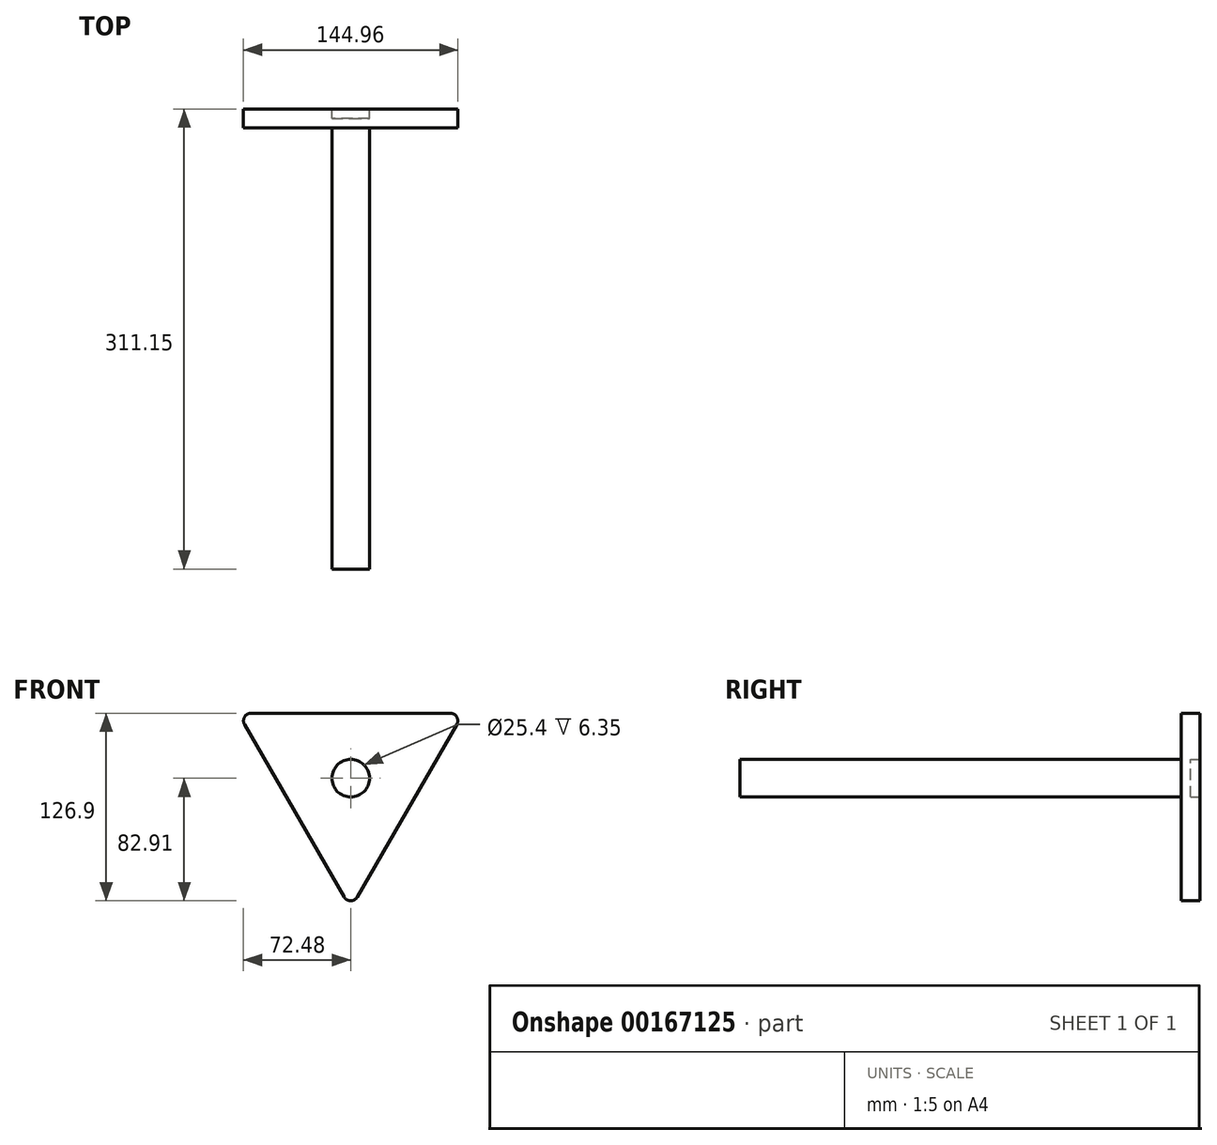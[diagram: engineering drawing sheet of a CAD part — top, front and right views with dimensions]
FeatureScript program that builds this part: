
annotation { "Feature Type Name" : "Feature", "Feature Type Description" : "" }
export const myFeature = defineFeature(function(context is Context, id is Id, definition is map)
    precondition{}
    {
        {
            var Q0;
            Q0=qCreatedBy(makeId("Front.planeOp"),FACE);
            var sketch = newSketch(context, id + "F0", { "sketchPlane" : qUnion([Q0])});
            skLineSegment(sketch, "E0.0", {"start": v(-76.2, 44) * mm, "end": v(76.2, 44) * mm});
            skLineSegment(sketch, "E0.1", {"start": v(76.2, 44) * mm, "end": v(0, -87.99) * mm});
            skLineSegment(sketch, "E0.2", {"start": v(0, -87.99) * mm, "end": v(-76.2, 44) * mm});
            skCircle(sketch, "E1", {"center": v(0, 0) * mm, "radius": 12.7 * mm});
            skSolve(sketch);
        }
        {
            var Q0;
            Q0=makeQuery(id+"F0.imprint","IMPRINT",FACE,{"disambiguationData":[TD([[makeQuery(id+"F0.imprint","IMPRINT",EDGE,{"derivedFrom":sQuery(id+"F0.wireOp",EDGE,"E0.0")}),-1.0]])]});
            extrude(context, id + "F1", {"entities" : qUnion([Q0]), "endBound" : BoundingType.SYMMETRIC, "depth" : 12.7 * mm});
        }
        {
            var Q0;
            Q0=makeQuery(id+"F1.opExtrude","SWEPT_EDGE",EDGE,{"disambiguationData":[OSD([sQuery(id+"F0.wireOp",EDGE,"E0.1"),sQuery(id+"F0.wireOp",EDGE,"E0.2")])]});
            var Q1;
            Q1=makeQuery(id+"F1.opExtrude","SWEPT_EDGE",EDGE,{"disambiguationData":[OSD([sQuery(id+"F0.wireOp",EDGE,"E0.0"),sQuery(id+"F0.wireOp",EDGE,"E0.1")])]});
            var Q2;
            Q2=makeQuery(id+"F1.opExtrude","SWEPT_EDGE",EDGE,{"disambiguationData":[OSD([sQuery(id+"F0.wireOp",EDGE,"E0.0"),sQuery(id+"F0.wireOp",EDGE,"E0.2")])]});
            fillet(context, id + "F2", {"entities" : qUnion([Q0, Q1, Q2]), "radius" : 5.08 * mm, "tangentPropagation" : true, "allowEdgeOverflow" : false});
        }
        {
            var Q0;
            Q0=makeQuery(id+"F0.imprint","IMPRINT",FACE,{"disambiguationData":[TD([[makeQuery(id+"F0.imprint","IMPRINT",EDGE,{"derivedFrom":sQuery(id+"F0.wireOp",EDGE,"E1")}),1.0]])]});
            extrude(context, id + "F3", {"entities" : qUnion([Q0]), "operationType" : NewBodyOperationType.ADD, "depth" : 304.8 * mm});
        }
    });
